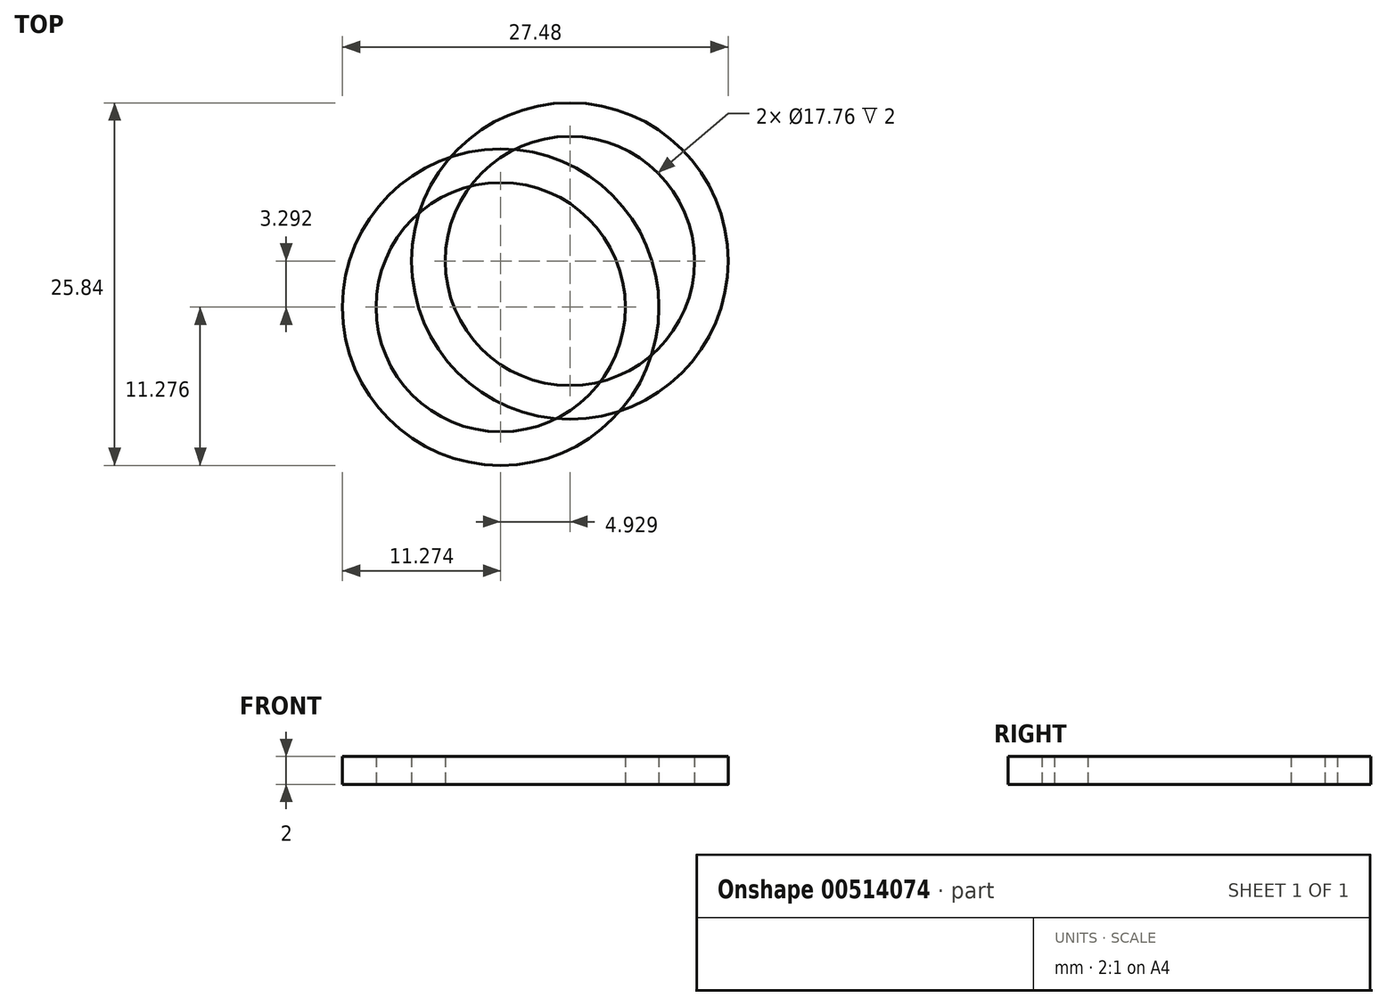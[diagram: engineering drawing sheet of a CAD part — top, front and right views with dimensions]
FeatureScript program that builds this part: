
annotation { "Feature Type Name" : "Feature", "Feature Type Description" : "" }
export const myFeature = defineFeature(function(context is Context, id is Id, definition is map)
    precondition{}
    {
        {
            var Q0;
            Q0=qCreatedBy(makeId("Top.planeOp"),FACE);
            var sketch = newSketch(context, id + "F0", { "sketchPlane" : qUnion([Q0])});
            skCircle(sketch, "E0", {"center": v(-21.28, 26.53) * mm, "radius": 8.88 * mm});
            skCircle(sketch, "E1", {"center": v(-21.28, 26.53) * mm, "radius": 11.27 * mm});
            skLineSegment(sketch, "E2", {"start": v(0, 0) * mm, "end": v(-21.28, 26.53) * mm, "construction": true});
            skSolve(sketch);
        }
        {
            var Q0;
            Q0=makeQuery(id+"F0.imprint","IMPRINT",FACE,{"disambiguationData":[TD([[makeQuery(id+"F0.imprint","IMPRINT",EDGE,{"derivedFrom":sQuery(id+"F0.wireOp",EDGE,"E0")}),-1.0]])]});
            extrude(context, id + "F1", {"entities" : qUnion([Q0]), "depth" : 2 * mm});
        }
        {
            var Q0;
            Q0=qCreatedBy(makeId("Right.planeOp"),FACE);
            var sketch = newSketch(context, id + "F2", { "sketchPlane" : qUnion([Q0])});
            skLineSegment(sketch, "E3", {"start": v(0, 0) * mm, "end": v(0, -51.4) * mm});
            skSolve(sketch);
        }
        {
            var Q0;
            Q0=makeQuery(id+"F1.opExtrude","SWEPT_BODY",BODY,{"disambiguationData":[OSD([sQuery(id+"F0.wireOp",EDGE,"E0"),sQuery(id+"F0.wireOp",EDGE,"E1")])]});
            var Q1;
            Q1=sQuery(id+"F2.wireOp",EDGE,"E3");
            circularPattern(context, id + "F3", {"entities" : qUnion([Q0]), "axis" : qUnion([Q1]), "angle" : 10 * degree, "instanceCount" : 2, "equalSpace" : true});
        }
    });
